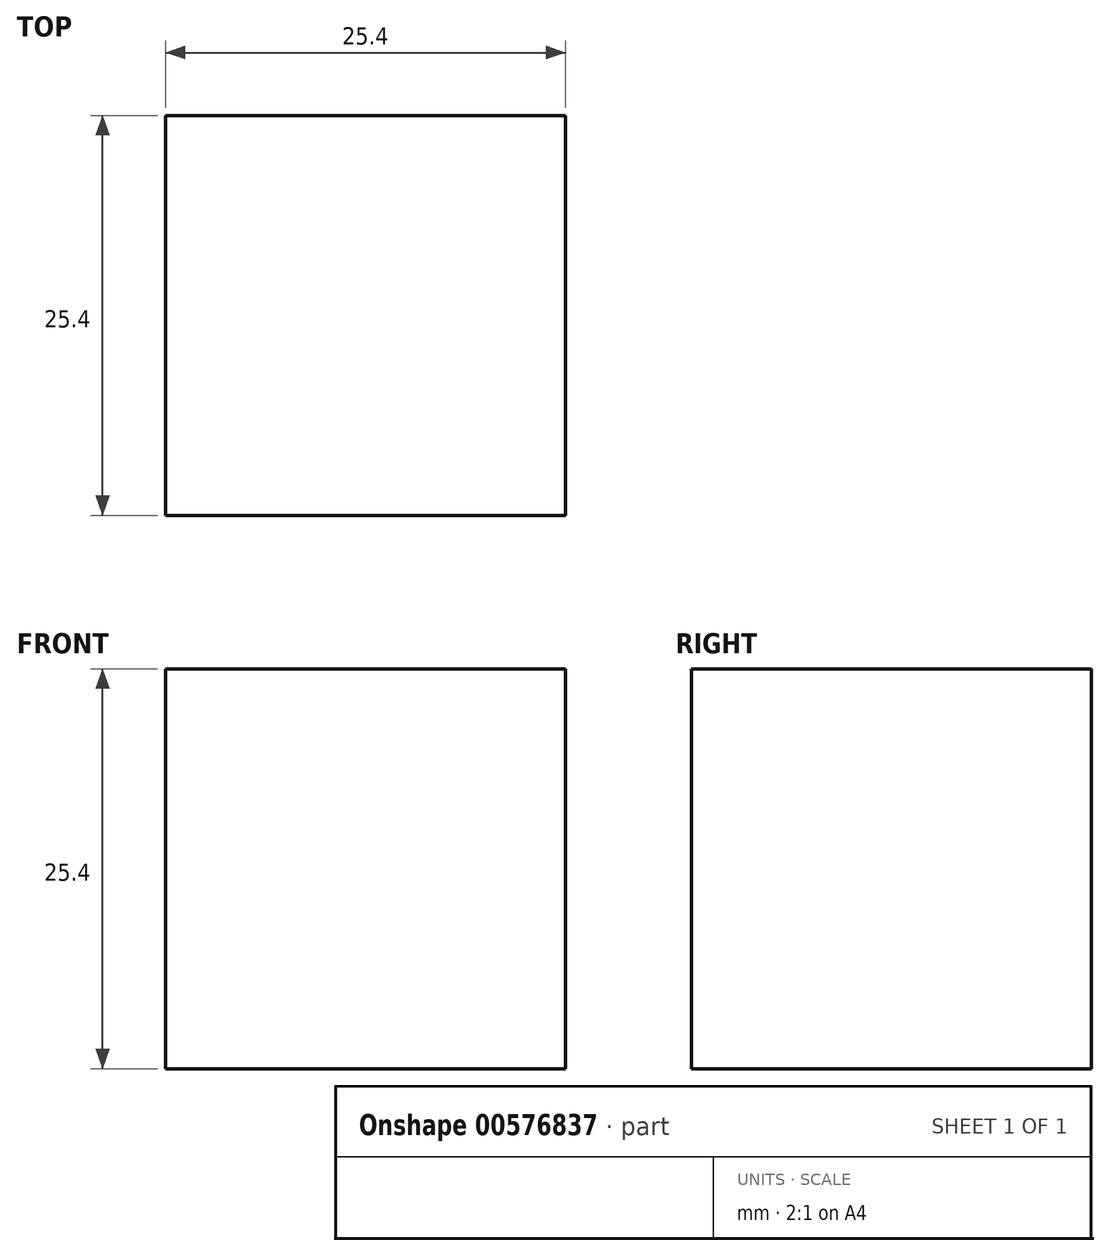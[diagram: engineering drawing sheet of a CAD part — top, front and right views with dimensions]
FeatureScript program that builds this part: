
annotation { "Feature Type Name" : "Feature", "Feature Type Description" : "" }
export const myFeature = defineFeature(function(context is Context, id is Id, definition is map)
    precondition{}
    {
        {
            var Q0;
            Q0=qCreatedBy(makeId("Front.planeOp"),FACE);
            var sketch = newSketch(context, id + "F0", { "sketchPlane" : qUnion([Q0])});
            skLineSegment(sketch, "E0.bottom", {"start": v(12.7, 12.7) * mm, "end": v(-12.7, 12.7) * mm});
            skLineSegment(sketch, "E0.top", {"start": v(12.7, -12.7) * mm, "end": v(-12.7, -12.7) * mm});
            skLineSegment(sketch, "E0.left", {"start": v(12.7, 12.7) * mm, "end": v(12.7, -12.7) * mm});
            skLineSegment(sketch, "E0.right", {"start": v(-12.7, 12.7) * mm, "end": v(-12.7, -12.7) * mm});
            skPoint(sketch, "E0.middle", {"position": v(0, 0) * mm});
            skSolve(sketch);
        }
        {
            var Q0;
            Q0=makeQuery(id+"F0.imprint","IMPRINT",FACE,{"disambiguationData":[TD([[makeQuery(id+"F0.imprint","IMPRINT",EDGE,{"derivedFrom":sQuery(id+"F0.wireOp",EDGE,"E0.bottom")}),1.0]])]});
            extrude(context, id + "F1", {"entities" : qUnion([Q0]), "depth" : 25.4 * mm, "offsetDistance" : 25.4 * mm});
        }
    });
